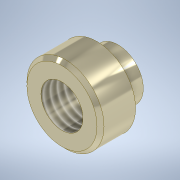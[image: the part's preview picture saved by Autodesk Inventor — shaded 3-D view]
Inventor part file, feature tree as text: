
AUTODESK INVENTOR PART (.ipt)
format: ipt  version: 2022 (Build 260153000, 153)  size: 127,488 bytes
history: native  units: mm
features: other x1, revolve x1, thread x1, chamfer x1, sketch x1
ambient origin geometry x8: Origin, YZ Plane, XZ Plane, XY Plane, X Axis, Y Axis, Z Axis, Center Point
bodies: Body1 (feature_tree)
feature tree (5):
  other  "Твердое тело1"
  revolve  "Вращение1"
  thread  "Резьба1"
  chamfer  "Фаска1"  Distance=2.75mm
  sketch  "Эскиз1"
